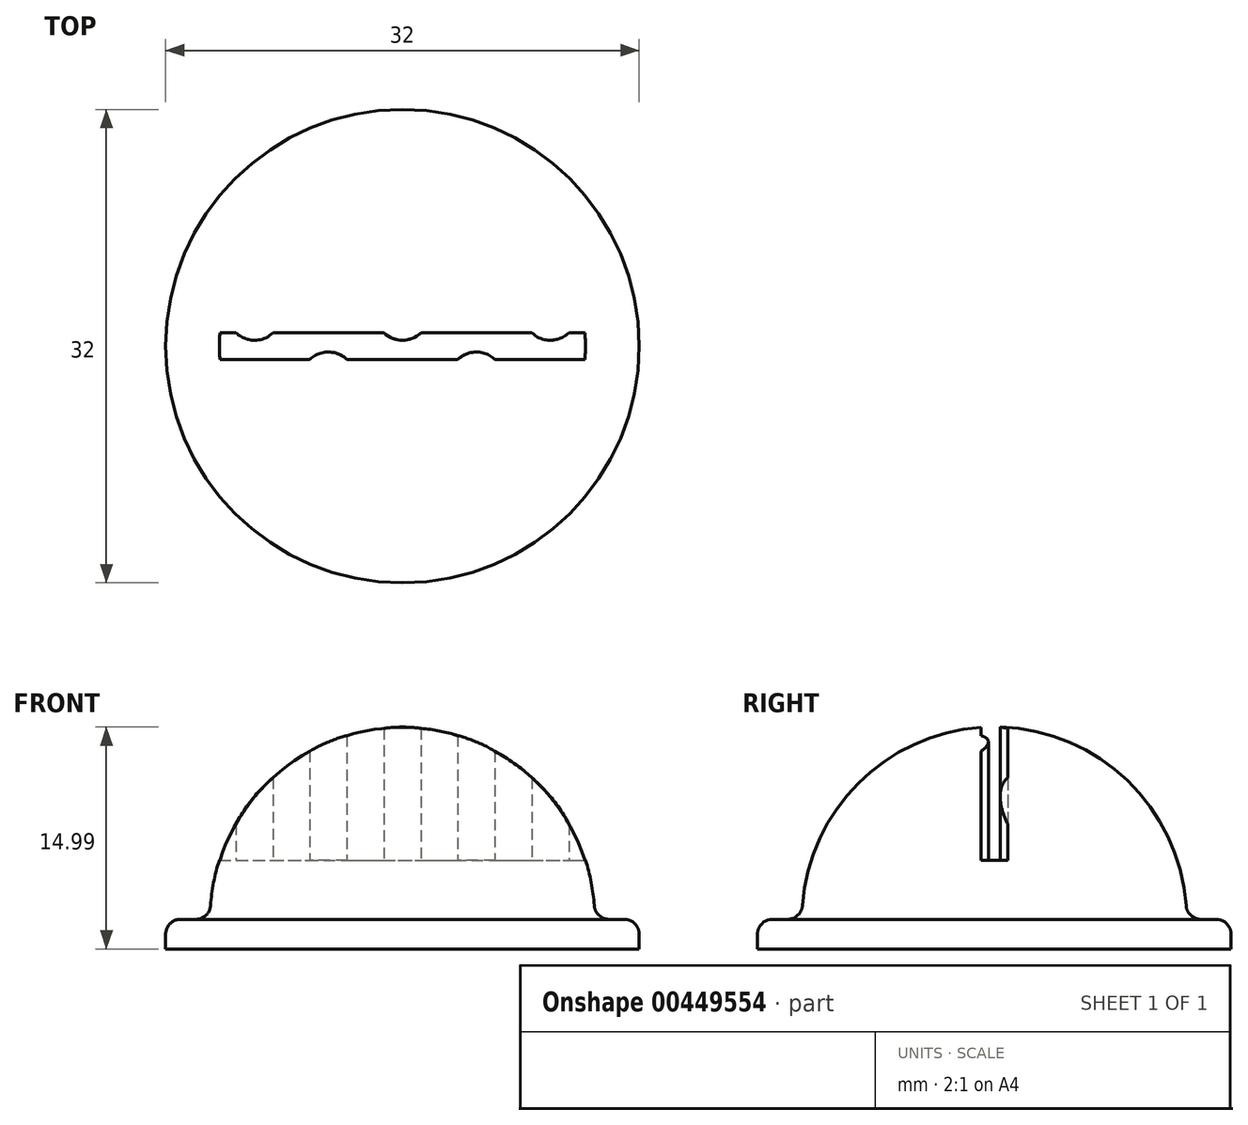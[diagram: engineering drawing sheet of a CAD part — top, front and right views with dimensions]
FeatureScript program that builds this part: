
annotation { "Feature Type Name" : "Feature", "Feature Type Description" : "" }
export const myFeature = defineFeature(function(context is Context, id is Id, definition is map)
    precondition{}
    {
        {
            var Q0;
            Q0=qCreatedBy(makeId("Front.planeOp"),FACE);
            var sketch = newSketch(context, id + "F0", { "sketchPlane" : qUnion([Q0])});
            skLineSegment(sketch, "E0.bottom", {"start": v(0, 0) * mm, "end": v(16, 0) * mm});
            skLineSegment(sketch, "E0.top", {"start": v(0, 2) * mm, "end": v(16, 2) * mm});
            skLineSegment(sketch, "E0.left", {"start": v(0, 0) * mm, "end": v(0, 2) * mm});
            skLineSegment(sketch, "E0.right", {"start": v(16, 0) * mm, "end": v(16, 2) * mm});
            skLineSegment(sketch, "E1", {"start": v(0, 2) * mm, "end": v(0, 15) * mm});
            skArc(sketch, "E2", {"start": v(13, 2) * mm, "mid": v(9.2, 11.2) * mm, "end": v(0, 15) * mm});
            skLineSegment(sketch, "E3", {"start": v(0, 15) * mm, "end": v(8.01, 15) * mm, "construction": true});
            skSolve(sketch);
        }
        {
            var Q0;
            Q0 = qSketchRegion(id + "F0", true);
            var Q1;
            Q1=sQuery(id+"F0.wireOp",EDGE,"E1");
            revolve(context, id + "F1", {"entities" : qUnion([Q0]), "axis" : qUnion([Q1]), "revolveType" : RevolveType.FULL});
        }
        {
            var Q0;
            Q0=makeQuery(id+"F1.opRevolve","SWEPT_EDGE",EDGE,{"disambiguationData":[OSD([sQuery(id+"F0.wireOp",EDGE,"E0.top"),sQuery(id+"F0.wireOp",EDGE,"E2")])]});
            var Q1;
            Q1=makeQuery(id+"F1.opRevolve","SWEPT_EDGE",EDGE,{"disambiguationData":[OSD([sQuery(id+"F0.wireOp",EDGE,"E0.top"),sQuery(id+"F0.wireOp",EDGE,"E0.right")])]});
            fillet(context, id + "F2", {"entities" : qUnion([Q0, Q1]), "radius" : 1 * mm, "tangentPropagation" : true, "allowEdgeOverflow" : false});
        }
        {
            var Q0;
            Q0=qCreatedBy(makeId("Right.planeOp"),FACE);
            var sketch = newSketch(context, id + "F3", { "sketchPlane" : qUnion([Q0])});
            skLineSegment(sketch, "E4.bottom", {"start": v(-0.9, 16) * mm, "end": v(0.9, 16) * mm});
            skLineSegment(sketch, "E4.top", {"start": v(-0.9, 6) * mm, "end": v(0.9, 6) * mm});
            skLineSegment(sketch, "E4.left", {"start": v(-0.9, 16) * mm, "end": v(-0.9, 6) * mm});
            skLineSegment(sketch, "E4.right", {"start": v(0.9, 16) * mm, "end": v(0.9, 6) * mm});
            skPoint(sketch, "E4.middle", {"position": v(0, 11) * mm});
            skSolve(sketch);
        }
        {
            var Q0;
            Q0 = qSketchRegion(id + "F3", true);
            extrude(context, id + "F4", {"entities" : qUnion([Q0]), "operationType" : NewBodyOperationType.REMOVE, "endBound" : BoundingType.THROUGH_ALL, "oppositeDirection" : true, "depth" : 25 * mm, "hasSecondDirection" : true, "secondDirectionOppositeDirection" : false, "secondDirectionDepth" : 25 * mm});
        }
        {
            var Q0;
            Q0=makeQuery(id+"F4.boolean.opBoolean","COPY",FACE,{"derivedFrom":makeQuery(id+"F4.opExtrude","SWEPT_FACE",FACE,{"disambiguationData":[OSD([sQuery(id+"F3.wireOp",EDGE,"E4.top")])]})});
            var sketch = newSketch(context, id + "F5", { "sketchPlane" : qUnion([Q0])});
            skArc(sketch, "E5", {"start": v(-1.25, 0.9) * mm, "mid": v(0, 0.4) * mm, "end": v(1.25, 0.9) * mm});
            skLineSegment(sketch, "E6", {"start": v(1.25, 0.9) * mm, "end": v(-1.25, 0.9) * mm});
            skArc(sketch, "E7", {"start": v(8.75, 0.9) * mm, "mid": v(10, 0.4) * mm, "end": v(11.25, 0.9) * mm});
            skLineSegment(sketch, "E8", {"start": v(11.25, 0.9) * mm, "end": v(8.75, 0.9) * mm});
            skArc(sketch, "E9", {"start": v(-11.25, 0.9) * mm, "mid": v(-10, 0.4) * mm, "end": v(-8.75, 0.9) * mm});
            skLineSegment(sketch, "E10", {"start": v(-8.75, 0.9) * mm, "end": v(-11.25, 0.9) * mm});
            skArc(sketch, "E11", {"start": v(6.25, -0.9) * mm, "mid": v(5, -0.4) * mm, "end": v(3.75, -0.9) * mm});
            skLineSegment(sketch, "E12", {"start": v(3.75, -0.9) * mm, "end": v(6.25, -0.9) * mm});
            skArc(sketch, "E13", {"start": v(-3.75, -0.9) * mm, "mid": v(-5, -0.4) * mm, "end": v(-6.25, -0.9) * mm});
            skLineSegment(sketch, "E14", {"start": v(-6.25, -0.9) * mm, "end": v(-3.75, -0.9) * mm});
            skSolve(sketch);
        }
        {
            var Q0;
            Q0 = qSketchRegion(id + "F5", true);
            var Q1;
            Q1=makeQuery(id+"F1.opRevolve","SWEPT_FACE",FACE,{"disambiguationData":[OSD([sQuery(id+"F0.wireOp",EDGE,"E2")])]});
            extrude(context, id + "F6", {"entities" : qUnion([Q0]), "operationType" : NewBodyOperationType.ADD, "endBound" : BoundingType.UP_TO_SURFACE, "endBoundEntityFace" : qUnion([Q1]), "depth" : 25 * mm});
        }
    });
